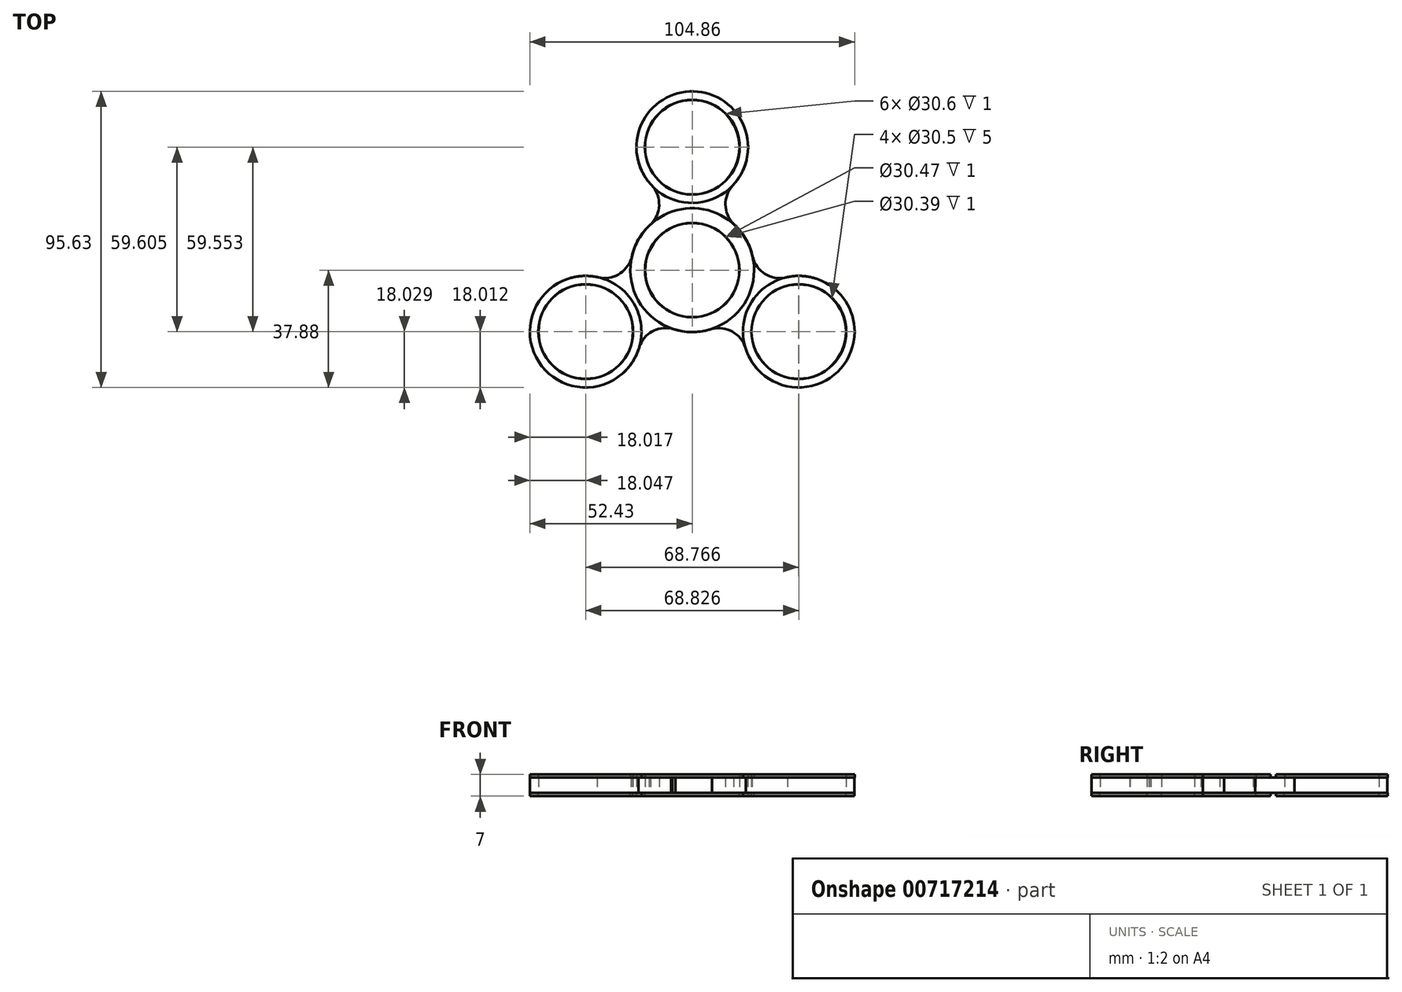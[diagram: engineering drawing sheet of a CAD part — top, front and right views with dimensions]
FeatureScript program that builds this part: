
annotation { "Feature Type Name" : "Feature", "Feature Type Description" : "" }
export const myFeature = defineFeature(function(context is Context, id is Id, definition is map)
    precondition{}
    {
        {
            var Q0;
            Q0=qCreatedBy(makeId("Top.planeOp"),FACE);
            var sketch = newSketch(context, id + "F0", { "sketchPlane" : qUnion([Q0])});
            skCircle(sketch, "E0", {"center": v(0, 39.7) * mm, "radius": 18 * mm});
            skCircle(sketch, "E1", {"center": v(0, 0) * mm, "radius": 20 * mm});
            skLineSegment(sketch, "E2.bottom", {"start": v(7.94, 23.58) * mm, "end": v(8, 23.58) * mm});
            skCircle(sketch, "E3", {"center": v(0, 39.7) * mm, "radius": 15.25 * mm});
            skCircle(sketch, "E4", {"center": v(0, 0) * mm, "radius": 15.25 * mm});
            skArc(sketch, "E5", {"start": v(13.4, 27.68) * mm, "mid": v(10.72, 21.32) * mm, "end": v(13.34, 14.93) * mm});
            skArc(sketch, "E6", {"start": v(-14, 14.29) * mm, "mid": v(-10.7, 20.92) * mm, "end": v(-13.48, 27.78) * mm});
            skArc(sketch, "E7.1.0", {"start": v(-5.38, -19.26) * mm, "mid": v(-12.77, -19.72) * mm, "end": v(-17.31, -25.56) * mm});
            skCircle(sketch, "E7.1.1", {"center": v(-34.38, -19.85) * mm, "radius": 18 * mm});
            skCircle(sketch, "E7.1.2", {"center": v(-34.38, -19.85) * mm, "radius": 15.25 * mm});
            skArc(sketch, "E7.1.3", {"start": v(-30.67, -2.24) * mm, "mid": v(-24.05, -1.5) * mm, "end": v(-19.75, 3.59) * mm});
            skArc(sketch, "E7.2.0", {"start": v(19.37, 4.97) * mm, "mid": v(23.46, -1.2) * mm, "end": v(30.8, -2.21) * mm});
            skCircle(sketch, "E7.2.1", {"center": v(34.38, -19.85) * mm, "radius": 18 * mm});
            skCircle(sketch, "E7.2.2", {"center": v(34.38, -19.85) * mm, "radius": 15.25 * mm});
            skArc(sketch, "E7.2.3", {"start": v(17.27, -25.44) * mm, "mid": v(13.14, -19.96) * mm, "end": v(6.34, -19) * mm});
            skLineSegment(sketch, "E8.bottom", {"start": v(-13.16, 27.42) * mm, "end": v(-13.13, 27.42) * mm});
            skLineSegment(sketch, "E8.top", {"start": v(-13.3, 14.93) * mm, "end": v(-13.28, 14.93) * mm});
            skLineSegment(sketch, "E9.bottom", {"start": v(-19.75, 3.59) * mm, "end": v(-19.7, 3.48) * mm});
            skLineSegment(sketch, "E9.top", {"start": v(-30.5, -2.27) * mm, "end": v(-30.5, -2.28) * mm});
            skLineSegment(sketch, "E10.bottom", {"start": v(6.34, -19) * mm, "end": v(6.36, -18.96) * mm});
            skLineSegment(sketch, "E10.top", {"start": v(17.1, -24.86) * mm, "end": v(17.1, -24.86) * mm});
            skLineSegment(sketch, "E11.trimOffspring", {"start": v(13.14, 27.42) * mm, "end": v(13.16, 27.42) * mm});
            skLineSegment(sketch, "E12.trimOffspring", {"start": v(13.3, 14.93) * mm, "end": v(13.34, 14.93) * mm});
            skPoint(sketch, "E13.orphan", {"position": v(-31.82, 0) * mm});
            skLineSegment(sketch, "E14.trimOffspring", {"start": v(-17.24, -25.26) * mm, "end": v(-17.22, -25.29) * mm});
            skLineSegment(sketch, "E15.trimOffspring", {"start": v(-6.83, -18.8) * mm, "end": v(-6.8, -18.86) * mm});
            skLineSegment(sketch, "E16.trimOffspring", {"start": v(30.07, -2.4) * mm, "end": v(30.08, -2.37) * mm});
            skLineSegment(sketch, "E17.trimOffspring", {"start": v(19.6, 3.96) * mm, "end": v(19.6, 3.97) * mm});
            skSolve(sketch);
        }
        {
            var Q0;
            Q0=qCreatedBy(makeId("Top.planeOp"),FACE);
            cPlane(context, id + "F1", {"entities" : qUnion([Q0]), "cplaneType" : CPlaneType.OFFSET, "offset" : 2.5 * mm, "width" : 152.4 * mm, "height" : 152.4 * mm});
        }
        {
            var Q0;
            Q0=qCreatedBy(id+"F1.planeOp",FACE);
            var sketch = newSketch(context, id + "F2", { "sketchPlane" : qUnion([Q0])});
            skCircle(sketch, "E18", {"center": v(0, 39.74) * mm, "radius": 15.3 * mm});
            skCircle(sketch, "E19", {"center": v(0, 39.74) * mm, "radius": 18.01 * mm});
            skCircle(sketch, "E20.1.0", {"center": v(-34.41, -19.87) * mm, "radius": 18.01 * mm});
            skCircle(sketch, "E20.1.1", {"center": v(-34.41, -19.87) * mm, "radius": 15.3 * mm});
            skCircle(sketch, "E20.2.0", {"center": v(34.41, -19.87) * mm, "radius": 18.01 * mm});
            skCircle(sketch, "E20.2.1", {"center": v(34.41, -19.87) * mm, "radius": 15.3 * mm});
            skPoint(sketch, "E20.center", {"position": v(0, 0) * mm});
            skCircle(sketch, "E21", {"center": v(0, 0) * mm, "radius": 15.23 * mm});
            skCircle(sketch, "E22", {"center": v(0, 0) * mm, "radius": 19.98 * mm});
            skSolve(sketch);
        }
        {
            var Q0;
            Q0=qCreatedBy(makeId("Top.planeOp"),FACE);
            cPlane(context, id + "F3", {"entities" : qUnion([Q0]), "cplaneType" : CPlaneType.OFFSET, "offset" : 2.5 * mm, "oppositeDirection" : true, "width" : 152.4 * mm, "height" : 152.4 * mm});
        }
        {
            var Q0;
            Q0=qCreatedBy(id+"F3.planeOp",FACE);
            var sketch = newSketch(context, id + "F4", { "sketchPlane" : qUnion([Q0])});
            skCircle(sketch, "E23", {"center": v(0, 39.72) * mm, "radius": 15.3 * mm});
            skCircle(sketch, "E24", {"center": v(0, 39.72) * mm, "radius": 18 * mm});
            skCircle(sketch, "E25.1.0", {"center": v(-34.4, -19.86) * mm, "radius": 18 * mm});
            skCircle(sketch, "E25.1.1", {"center": v(-34.4, -19.86) * mm, "radius": 15.3 * mm});
            skCircle(sketch, "E25.2.0", {"center": v(34.4, -19.86) * mm, "radius": 18 * mm});
            skCircle(sketch, "E25.2.1", {"center": v(34.4, -19.86) * mm, "radius": 15.3 * mm});
            skPoint(sketch, "E25.center", {"position": v(0, 0) * mm});
            skCircle(sketch, "E26", {"center": v(0, 0) * mm, "radius": 15.2 * mm});
            skCircle(sketch, "E27", {"center": v(0, 0) * mm, "radius": 19.99 * mm});
            skSolve(sketch);
        }
        {
            var Q0;
            Q0=makeQuery(id+"F0.imprint","IMPRINT",FACE,{"disambiguationData":[TD([[makeQuery(id+"F0.imprint","IMPRINT",EDGE,{"derivedFrom":sQuery(id+"F0.wireOp",EDGE,"E3")}),-1.0]])]});
            var Q1;
            {var subQ0=sQuery(id+"F0.wireOp",EDGE,"E12.trimOffspring");Q1=makeQuery(id+"F0.imprint","IMPRINT",FACE,{"disambiguationData":[TD([[makeQuery(id+"F0.imprint","IMPRINT",EDGE,{"derivedFrom":subQ0}),1.0]])]});}
            var Q2;
            Q2=makeQuery(id+"F0.imprint","IMPRINT",FACE,{"disambiguationData":[TD([[makeQuery(id+"F0.imprint","IMPRINT",EDGE,{"derivedFrom":sQuery(id+"F0.wireOp",EDGE,"E4")}),-1.0]])]});
            var Q3;
            {var subQ0=sQuery(id+"F0.wireOp",EDGE,"E9.bottom");Q3=makeQuery(id+"F0.imprint","IMPRINT",FACE,{"disambiguationData":[TD([[makeQuery(id+"F0.imprint","IMPRINT",EDGE,{"derivedFrom":subQ0}),-1.0]])]});}
            var Q4;
            Q4=makeQuery(id+"F0.imprint","IMPRINT",FACE,{"disambiguationData":[TD([[makeQuery(id+"F0.imprint","IMPRINT",EDGE,{"derivedFrom":sQuery(id+"F0.wireOp",EDGE,"E7.1.2")}),-1.0]])]});
            var Q5;
            {var subQ5=sQuery(id+"F0.wireOp",EDGE,"E10.bottom");Q5=makeQuery(id+"F0.imprint","IMPRINT",FACE,{"disambiguationData":[TD([[makeQuery(id+"F0.imprint","IMPRINT",EDGE,{"derivedFrom":subQ5}),-1.0]])]});}
            var Q6;
            Q6=makeQuery(id+"F0.imprint","IMPRINT",FACE,{"disambiguationData":[TD([[makeQuery(id+"F0.imprint","IMPRINT",EDGE,{"derivedFrom":sQuery(id+"F0.wireOp",EDGE,"E7.2.2")}),-1.0]])]});
            extrude(context, id + "F5", {"entities" : qUnion([Q0, Q1, Q2, Q3, Q4, Q5, Q6]), "endBound" : BoundingType.SYMMETRIC, "depth" : 5 * mm, "offsetDistance" : 25.4 * mm});
        }
        {
            var Q0;
            Q0=makeQuery(id+"F4.imprint","IMPRINT",FACE,{"disambiguationData":[TD([[makeQuery(id+"F4.imprint","IMPRINT",EDGE,{"derivedFrom":sQuery(id+"F4.wireOp",EDGE,"E23")}),-1.0]])]});
            var Q1;
            Q1=makeQuery(id+"F4.imprint","IMPRINT",FACE,{"disambiguationData":[TD([[makeQuery(id+"F4.imprint","IMPRINT",EDGE,{"derivedFrom":sQuery(id+"F4.wireOp",EDGE,"E25.2.0")}),1.0]])]});
            var Q2;
            Q2=makeQuery(id+"F4.imprint","IMPRINT",FACE,{"disambiguationData":[TD([[makeQuery(id+"F4.imprint","IMPRINT",EDGE,{"derivedFrom":sQuery(id+"F4.wireOp",EDGE,"E25.1.0")}),1.0]])]});
            extrude(context, id + "F6", {"entities" : qUnion([Q0, Q1, Q2]), "operationType" : NewBodyOperationType.ADD, "oppositeDirection" : true, "depth" : 1 * mm, "offsetDistance" : 25.4 * mm});
        }
        {
            var Q0;
            Q0=makeQuery(id+"F2.imprint","IMPRINT",FACE,{"disambiguationData":[TD([[makeQuery(id+"F2.imprint","IMPRINT",EDGE,{"derivedFrom":sQuery(id+"F2.wireOp",EDGE,"E18")}),-1.0]])]});
            var Q1;
            Q1=makeQuery(id+"F2.imprint","IMPRINT",FACE,{"disambiguationData":[TD([[makeQuery(id+"F2.imprint","IMPRINT",EDGE,{"derivedFrom":sQuery(id+"F2.wireOp",EDGE,"E20.1.0")}),1.0]])]});
            var Q2;
            Q2=makeQuery(id+"F2.imprint","IMPRINT",FACE,{"disambiguationData":[TD([[makeQuery(id+"F2.imprint","IMPRINT",EDGE,{"derivedFrom":sQuery(id+"F2.wireOp",EDGE,"E20.2.0")}),1.0]])]});
            extrude(context, id + "F7", {"entities" : qUnion([Q0, Q1, Q2]), "operationType" : NewBodyOperationType.ADD, "depth" : 1 * mm, "offsetDistance" : 25.4 * mm});
        }
        {
            var Q0;
            Q0=makeQuery(id+"F2.imprint","IMPRINT",FACE,{"disambiguationData":[TD([[makeQuery(id+"F2.imprint","IMPRINT",EDGE,{"derivedFrom":sQuery(id+"F2.wireOp",EDGE,"E21")}),-1.0]])]});
            extrude(context, id + "F8", {"entities" : qUnion([Q0]), "operationType" : NewBodyOperationType.ADD, "depth" : 1 * mm, "offsetDistance" : 25.4 * mm});
        }
        {
            var Q0;
            Q0=makeQuery(id+"F4.imprint","IMPRINT",FACE,{"disambiguationData":[TD([[makeQuery(id+"F4.imprint","IMPRINT",EDGE,{"derivedFrom":sQuery(id+"F4.wireOp",EDGE,"E26")}),-1.0]])]});
            extrude(context, id + "F9", {"entities" : qUnion([Q0]), "operationType" : NewBodyOperationType.ADD, "oppositeDirection" : true, "depth" : 1 * mm, "offsetDistance" : 25.4 * mm});
        }
    });
